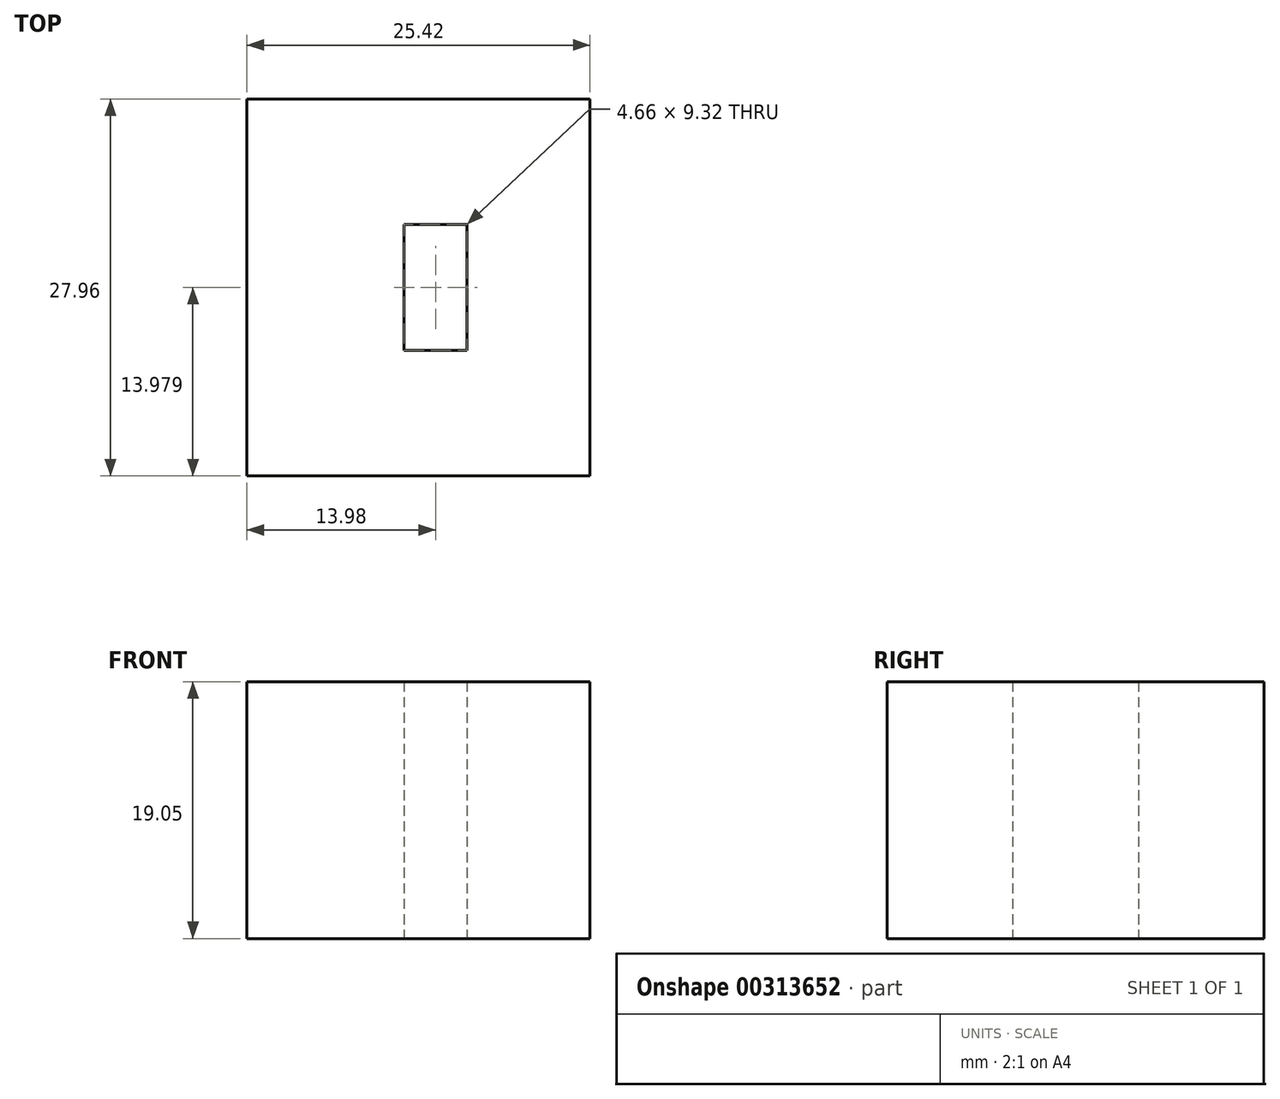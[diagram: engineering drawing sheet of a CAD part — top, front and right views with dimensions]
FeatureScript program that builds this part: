
annotation { "Feature Type Name" : "Feature", "Feature Type Description" : "" }
export const myFeature = defineFeature(function(context is Context, id is Id, definition is map)
    precondition{}
    {
        {
            var Q0;
            Q0=qCreatedBy(makeId("Top.planeOp"),FACE);
            var sketch = newSketch(context, id + "F0", { "sketchPlane" : qUnion([Q0])});
            skLineSegment(sketch, "E0.bottom", {"start": v(-50.42, 33.26) * mm, "end": v(-25, 33.26) * mm});
            skLineSegment(sketch, "E0.top", {"start": v(-50.42, 5.3) * mm, "end": v(-25, 5.3) * mm});
            skLineSegment(sketch, "E0.left", {"start": v(-50.42, 33.26) * mm, "end": v(-50.42, 5.3) * mm});
            skLineSegment(sketch, "E0.right", {"start": v(-25, 33.26) * mm, "end": v(-25, 5.3) * mm});
            skLineSegment(sketch, "E1.bottom", {"start": v(-34.1, 23.94) * mm, "end": v(-38.77, 23.94) * mm});
            skLineSegment(sketch, "E1.top", {"start": v(-34.1, 14.62) * mm, "end": v(-38.77, 14.62) * mm});
            skLineSegment(sketch, "E1.left", {"start": v(-34.1, 23.94) * mm, "end": v(-34.1, 14.62) * mm});
            skLineSegment(sketch, "E1.right", {"start": v(-38.77, 23.94) * mm, "end": v(-38.77, 14.62) * mm});
            skSolve(sketch);
        }
        {
            var Q0;
            Q0 = qSketchRegion(id + "F0", true);
            extrude(context, id + "F1", {"entities" : qUnion([Q0]), "depth" : 6.35 * mm});
        }
        {
            var Q0;
            Q0 = qSketchRegion(id + "F0", true);
            extrude(context, id + "F2", {"entities" : qUnion([Q0]), "operationType" : NewBodyOperationType.ADD, "depth" : 19.05 * mm});
        }
    });
